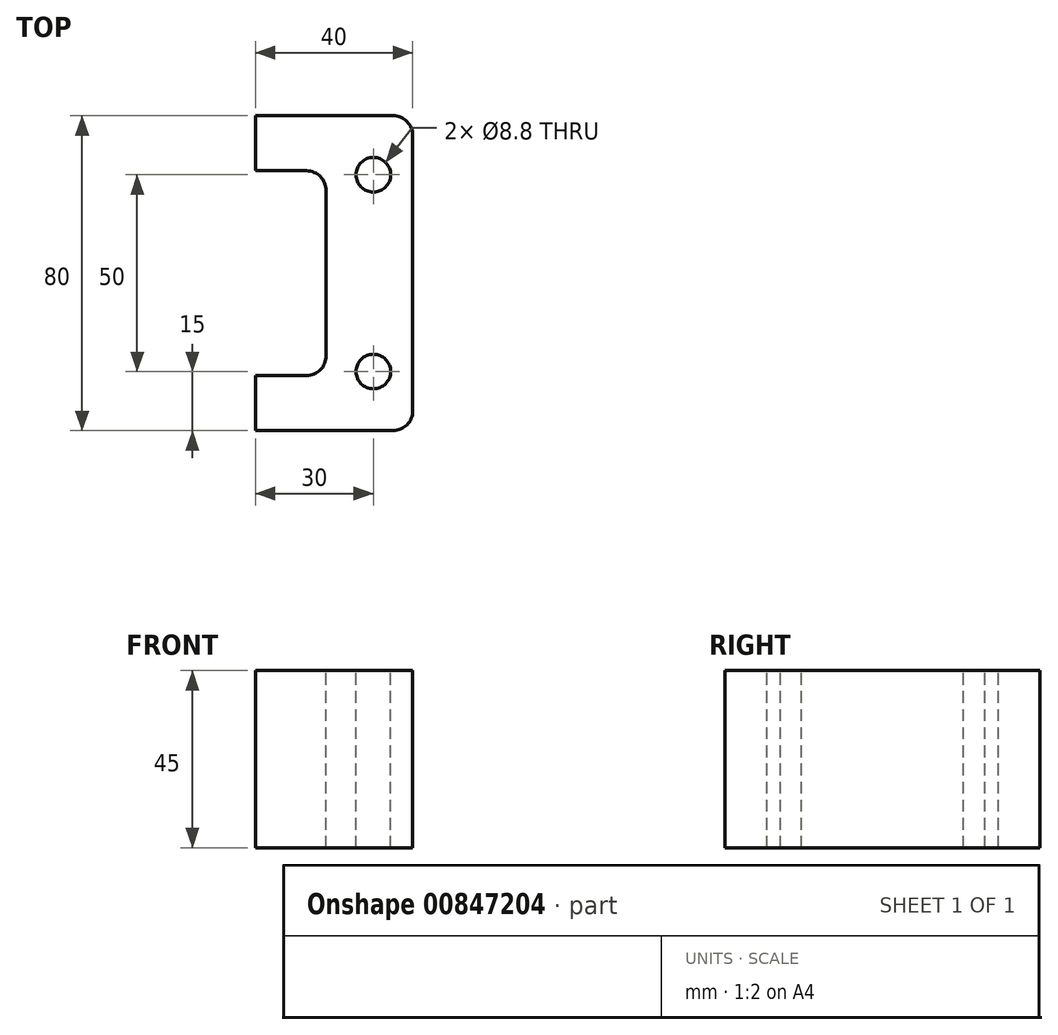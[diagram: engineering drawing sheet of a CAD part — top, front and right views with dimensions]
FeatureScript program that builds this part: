
annotation { "Feature Type Name" : "Feature", "Feature Type Description" : "" }
export const myFeature = defineFeature(function(context is Context, id is Id, definition is map)
    precondition{}
    {
        {
            var Q0;
            Q0=qCreatedBy(makeId("Top.planeOp"),FACE);
            var sketch = newSketch(context, id + "F0", { "sketchPlane" : qUnion([Q0])});
            skLineSegment(sketch, "E0.bottom", {"start": v(0, 0) * mm, "end": v(40, 0) * mm});
            skLineSegment(sketch, "E0.top", {"start": v(0, 80) * mm, "end": v(40, 80) * mm});
            skLineSegment(sketch, "E0.left", {"start": v(0, 0) * mm, "end": v(0, 80) * mm});
            skLineSegment(sketch, "E0.right", {"start": v(40, 0) * mm, "end": v(40, 80) * mm});
            skSolve(sketch);
        }
        {
            var Q0;
            Q0 = qSketchRegion(id + "F0", true);
            extrude(context, id + "F1", {"entities" : qUnion([Q0]), "depth" : 45 * mm, "offsetDistance" : 25 * mm});
        }
        {
            var Q0;
            Q0=makeQuery(id+"F1.opExtrude","CAP_FACE",FACE,{"disambiguationData":[OSD([sQuery(id+"F0.wireOp",EDGE,"E0.bottom"),sQuery(id+"F0.wireOp",EDGE,"E0.top"),sQuery(id+"F0.wireOp",EDGE,"E0.left"),sQuery(id+"F0.wireOp",EDGE,"E0.right")])],"isStart":false});
            var sketch = newSketch(context, id + "F2", { "sketchPlane" : qUnion([Q0])});
            skPoint(sketch, "E1", {"position": v(30, 15) * mm});
            skPoint(sketch, "E2", {"position": v(30, 65) * mm});
            skLineSegment(sketch, "E3", {"start": v(30, 15) * mm, "end": v(30, 65) * mm, "construction": true});
            skLineSegment(sketch, "E4", {"start": v(30, 40) * mm, "end": v(40, 40) * mm, "construction": true});
            skSolve(sketch);
        }
        {
            var Q0;
            Q0=sQuery(id+"F2.wireOp",VERTEX,"E2");
            var Q1;
            Q1=sQuery(id+"F2.wireOp",VERTEX,"E1");
            var Q2;
            Q2=makeQuery(id+"F1.opExtrude","SWEPT_BODY",BODY,{"disambiguationData":[OSD([sQuery(id+"F0.wireOp",EDGE,"E0.bottom"),sQuery(id+"F0.wireOp",EDGE,"E0.top"),sQuery(id+"F0.wireOp",EDGE,"E0.left"),sQuery(id+"F0.wireOp",EDGE,"E0.right")])]});
            hole(context, id + "F3", {"style" : HoleStyle.SIMPLE, "endStyle" : HoleEndStyle.THROUGH, "standardTappedOrClearance" : lookupTablePath({ "fit" : "Normal", "standard" : "ISO", "size" : "M8", "type" : "Clearance" }), "standardBlindInLast" : lookupTablePath({ "fit" : "Standard", "standard" : "ISO", "size" : "M8", "type" : "Clearance" }), "holeDiameter" : 8.8 * mm, "majorDiameter" : 5 * mm, "isTappedThrough" : true, "tappedDepth" : 12 * mm, "tapClearance" : 3, "locations" : qUnion([Q0, Q1]), "scope" : qUnion([Q2])});
        }
        {
            var Q0;
            Q0=makeQuery(id+"F1.opExtrude","CAP_FACE",FACE,{"disambiguationData":[OSD([sQuery(id+"F0.wireOp",EDGE,"E0.bottom"),sQuery(id+"F0.wireOp",EDGE,"E0.top"),sQuery(id+"F0.wireOp",EDGE,"E0.left"),sQuery(id+"F0.wireOp",EDGE,"E0.right")])],"isStart":false});
            var sketch = newSketch(context, id + "F4", { "sketchPlane" : qUnion([Q0])});
            skLineSegment(sketch, "E5.bottom", {"start": v(0, 66) * mm, "end": v(18, 66) * mm});
            skLineSegment(sketch, "E5.top", {"start": v(0, 14) * mm, "end": v(18, 14) * mm});
            skLineSegment(sketch, "E5.left", {"start": v(0, 66) * mm, "end": v(0, 14) * mm});
            skLineSegment(sketch, "E5.right", {"start": v(18, 66) * mm, "end": v(18, 14) * mm});
            skSolve(sketch);
        }
        {
            var Q0;
            Q0=makeQuery(id+"F4.imprint","IMPRINT",FACE,{"disambiguationData":[TD([[makeQuery(id+"F4.imprint","IMPRINT",EDGE,{"derivedFrom":sQuery(id+"F4.wireOp",EDGE,"E5.bottom")}),-1.0]])]});
            extrude(context, id + "F5", {"entities" : qUnion([Q0]), "operationType" : NewBodyOperationType.REMOVE, "endBound" : BoundingType.UP_TO_NEXT, "oppositeDirection" : true, "depth" : 25 * mm, "offsetDistance" : 25 * mm});
        }
        {
            var Q0;
            Q0=makeQuery(id+"F1.opExtrude","SWEPT_EDGE",EDGE,{"disambiguationData":[OSD([sQuery(id+"F0.wireOp",EDGE,"E0.bottom"),sQuery(id+"F0.wireOp",EDGE,"E0.right")])]});
            var Q1;
            Q1=makeQuery(id+"F1.opExtrude","SWEPT_EDGE",EDGE,{"disambiguationData":[OSD([sQuery(id+"F0.wireOp",EDGE,"E0.top"),sQuery(id+"F0.wireOp",EDGE,"E0.right")])]});
            var Q2;
            Q2=makeQuery(id+"F5.boolean.opBoolean","COPY",EDGE,{"derivedFrom":makeQuery(id+"F5.opExtrude","SWEPT_EDGE",EDGE,{"disambiguationData":[OSD([sQuery(id+"F4.wireOp",EDGE,"E5.top"),sQuery(id+"F4.wireOp",EDGE,"E5.right")])]})});
            var Q3;
            Q3=makeQuery(id+"F5.boolean.opBoolean","COPY",EDGE,{"derivedFrom":makeQuery(id+"F5.opExtrude","SWEPT_EDGE",EDGE,{"disambiguationData":[OSD([sQuery(id+"F4.wireOp",EDGE,"E5.bottom"),sQuery(id+"F4.wireOp",EDGE,"E5.right")])]})});
            fillet(context, id + "F6", {"entities" : qUnion([Q0, Q1, Q2, Q3]), "radius" : 5 * mm, "tangentPropagation" : true, "allowEdgeOverflow" : false});
        }
    });
